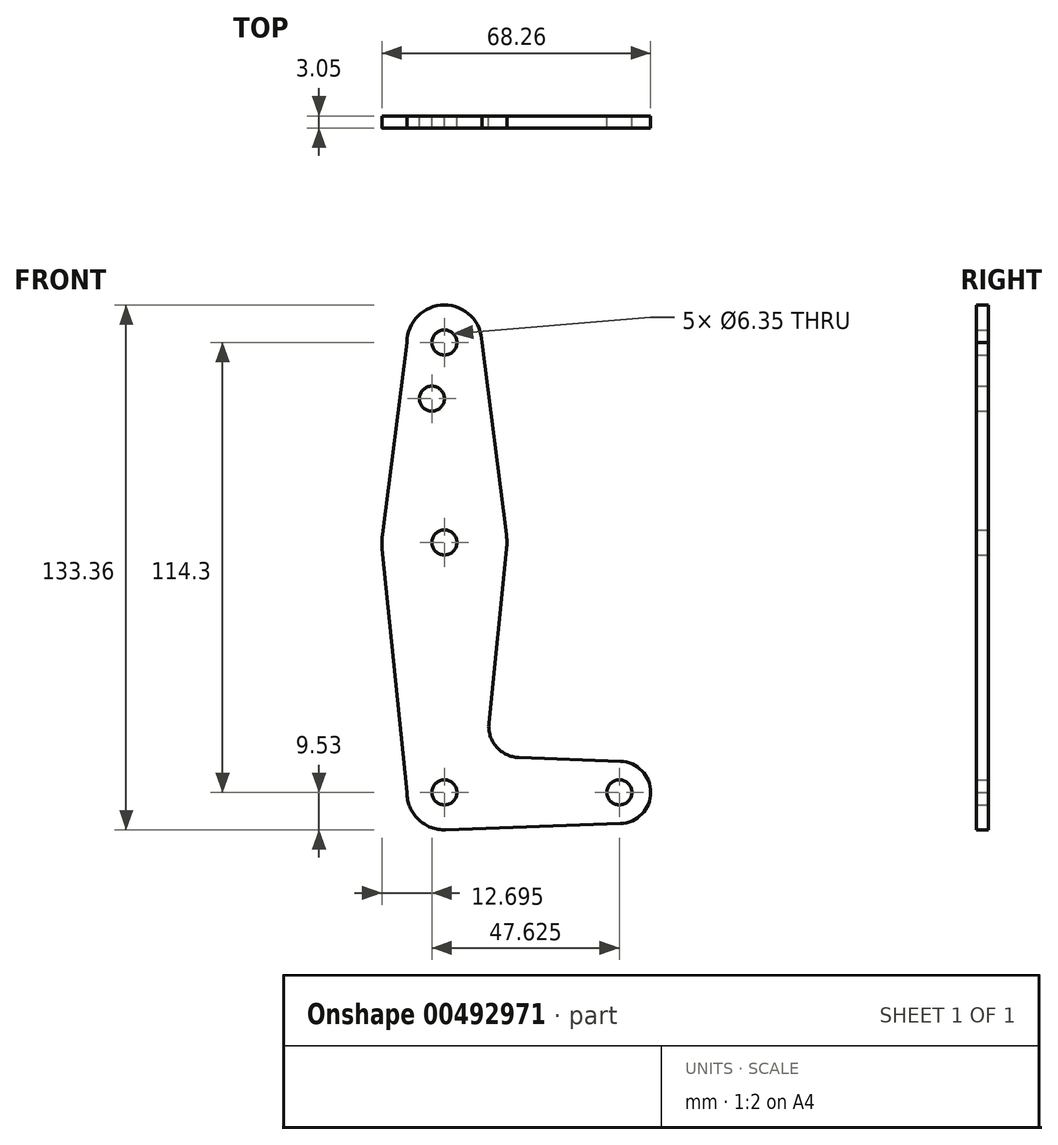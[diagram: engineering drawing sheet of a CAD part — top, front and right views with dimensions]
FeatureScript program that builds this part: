
annotation { "Feature Type Name" : "Feature", "Feature Type Description" : "" }
export const myFeature = defineFeature(function(context is Context, id is Id, definition is map)
    precondition{}
    {
        {
            var Q0;
            Q0=qCreatedBy(makeId("Front.planeOp"),FACE);
            var sketch = newSketch(context, id + "F0", { "sketchPlane" : qUnion([Q0])});
            skLineSegment(sketch, "E0", {"start": v(0, 0) * mm, "end": v(0, 114.3) * mm, "construction": true});
            skLineSegment(sketch, "E1", {"start": v(0, 0) * mm, "end": v(44.45, 0) * mm, "construction": true});
            skCircle(sketch, "E2", {"center": v(0, 0) * mm, "radius": 9.53 * mm});
            skCircle(sketch, "E3", {"center": v(44.45, 0) * mm, "radius": 7.94 * mm});
            skCircle(sketch, "E4", {"center": v(0, 114.3) * mm, "radius": 9.53 * mm});
            skCircle(sketch, "E5", {"center": v(0, 63.5) * mm, "radius": 15.88 * mm});
            skLineSegment(sketch, "E6", {"start": v(0, 63.5) * mm, "end": v(0, 0) * mm});
            skLineSegment(sketch, "E7", {"start": v(-9.53, 114.3) * mm, "end": v(-15.75, 65.5) * mm});
            skLineSegment(sketch, "E8", {"start": v(-9.53, 0) * mm, "end": v(-15.8, 61.9) * mm});
            skLineSegment(sketch, "E9", {"start": v(11.3, 17.6) * mm, "end": v(15.8, 61.9) * mm});
            skLineSegment(sketch, "E10", {"start": v(9.53, 114.3) * mm, "end": v(15.75, 65.5) * mm});
            skLineSegment(sketch, "E11", {"start": v(18.93, 8.85) * mm, "end": v(44.73, 7.93) * mm});
            skLineSegment(sketch, "E12", {"start": v(44.73, 7.93) * mm, "end": v(44.73, -7.93) * mm});
            skLineSegment(sketch, "E13", {"start": v(44.73, -7.93) * mm, "end": v(0, -9.53) * mm});
            skCircle(sketch, "E14", {"center": v(0, 114.3) * mm, "radius": 3.18 * mm});
            skCircle(sketch, "E15", {"center": v(0, 63.5) * mm, "radius": 3.18 * mm});
            skCircle(sketch, "E16", {"center": v(0, 0) * mm, "radius": 3.18 * mm});
            skCircle(sketch, "E17", {"center": v(44.45, 0) * mm, "radius": 3.18 * mm});
            skCircle(sketch, "E18", {"center": v(-3.18, 100.03) * mm, "radius": 3.18 * mm});
            skArc(sketch, "E19.filletArc", {"start": v(11.3, 17.6) * mm, "mid": v(13.22, 11.57) * mm, "end": v(18.93, 8.85) * mm});
            skSolve(sketch);
        }
        {
            var Q0;
            Q0 = qSketchRegion(id + "F0", true);
            extrude(context, id + "F1", {"entities" : qUnion([Q0]), "depth" : 3.05 * mm});
        }
    });
